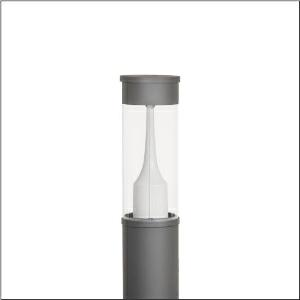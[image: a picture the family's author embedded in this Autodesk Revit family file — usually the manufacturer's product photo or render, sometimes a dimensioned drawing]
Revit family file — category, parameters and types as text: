
# Revit family: city-light_120_iq___p1_0a_5xa5285ff14h_303b
name_source: partatom
category: Lighting Fixtures
units: mm (PartAtom-declared; Revit-internal decimal feet)

## family parameters
Cut with Voids When Loaded = No
Host = Face
Light Source = No
Part Type = Normal
Room Calculation Point = No
Round Connector Dimension = Use Diameter
Shared = No

## types (1)
- --- (1 x LED, 1510 lm, 10.5 W, 3000K)
    Apparent Load = 11 VA
    CIE Flux Codes = 32 61 90 93 100
    Color Rendering = 70
    Color Temperature = 3000K
    Default Elevation = 1800 mm
    Description = City-Light 120 iQ, bollard luminaire, Module 540 iQ-SR, primary light control with 3 zone facetted reflector, of plastic, silver coated, highly specular, structured, primary optical cover: cover, of PMMA, transparent, light distribution: P1.0a, primary light characteristic: strongly asymmetric, LED, High Power LED, rated luminous flux: 1.510lm, luminous efficacy: 144lm/W, light colour: 730, colour temperature: 3000K, control gear: iQ Street-Remote, control: Auto-Match, Temp-Guard, Lumen-Switch, Night-Set, Smart-Wire, Light-Fading, Desk-Remote (wireless, voltage-free reading and setting of iQ features in the workshop via application-optimized NFC function/RFID function), optimised constant luminous flux control (CLO 2.0), Street-Remote, pre-setting: logarithmic dimming characteristic, with terminal, 6-pole, max. 2.5mm², mains connection: 230..240V, AC, 50/60Hz, start of lifetime: 11W, end of service life: 11W, reduction: 5W, luminaire housing, cylindrical, of extruded aluminium section, coated, Siteco® metallic grey (DB 702S), length: 1.200mm, diameter: 200mm, Module 540 iQ-SR, traffic white (RAL 9016), equipment: standard, protection rating (complete): IP54, insulation class (complete): insulation class II (safety insulation), certification: CE, ENEC, VDE, packaging unit: 1 piece

Light Distribution: P1.0a
    Height = 500 mm
    Lamp = 1 x LED
    Lamp Light Flux = 1510 lm
    Lamp Power = 10.5 W
    Lamp count = 1
    Length = 200 mm  [stored 0.656168 ft]
    Luminous efficacy = 144 lm/W
    Manufacturer = Siteco
    ModVariant = No
    Model = 5XA5285FF14H
    Mounting Place = Floor
    Mounting Type = Freestanding
    Number of Poles = 1
    OnlyDefault = Yes
    Power Factor = 1
    Product Name = City-Light 120 iQ | P1.0a
    Product group = bollard luminaire
    ProductGroupID = 1304
    Protection Class = Protection class II
    Protection Degree = IP 54
    RLX_Detail_Level = 1
    RLX_Emergency_Light_Flux = 0 lm
    RLX_Emergency_Type = 0
    RLX_Emergency_Type_DB = No
    RlxData = <blob elided: 52585 chars, md5=337056ba>
    Socket = socket
    Standby Power = 0 W
    System Light Flux = 1510 lm
    System Power = 11 W
    Type Comments = factory setting: luminous flux: 100 % | dim-lin: 254 | 419 mA
    Type Image = l_1006922.jpg
    URL = http://relux.com
    VarID = @adj_160629
    Voltage = 0 V
    Weight = 0.00 kg
    Width = 0 mm  [stored 0 ft]

note: [stored X ft] marks values corroborated as IEEE doubles in the binary element streams (Revit-internal decimal feet)

## geometry (parser evidence)
native form markers: Blend x4, Sweep x11
no freeform markers — native parametric forms only
